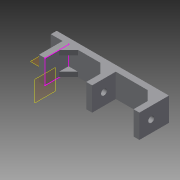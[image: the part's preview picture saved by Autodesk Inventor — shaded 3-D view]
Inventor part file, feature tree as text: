
AUTODESK INVENTOR PART (.ipt)
format: ipt  version: 2013 (Build 170138000, 138)  size: 146,944 bytes
history: native  units: in
note: dims shown in document units (in); Inventor stores cm internally (conversion verified against a paired STEP export)
features: sketch x6, extrude x5, plane x2
ambient origin geometry x8: Origin, YZ Plane, XZ Plane, XY Plane, X Axis, Y Axis, Z Axis, Center Point
bodies: Solid1 (feature_tree)
feature tree (13):
  extrude  "Extrusion1"  Depth=4.75in
  plane  "Work Plane1"
  extrude  "Extrusion3"  Depth=0.25in TaperAngle=0.0deg
  plane  "Work Plane2"
  sketch  "Sketch4"  dims[d8=0.5in d9=0.25in]
  extrude  "Extrusion4"  Depth=0.25in
  extrude  "Extrusion5"  Depth=1.75in
  extrude  "Extrusion6"  Depth=1.0in
  sketch  "Sketch1"  dims[d0=1.0in d1=4.75in]
  sketch  "Sketch3"  dims[d2=1.0in d3=0.25in d4=0.0in]
  sketch  "Sketch5"  dims[d10=1.0in d11=1.75in]
  sketch  "Sketch6"  dims[d12=0.25in d13=1.0in]
  sketch  "Sketch7"  dims[d14=1.75in d15=1.0in d16=0.0in d17=0.75in d18=0.5in d19=0.25in d20=3.0in d21=0.0in d22=0.4in d23=0.4in d24=0.4in d25=0.4in d26=0.2in d27=0.0in d28=0.4in d29=0.4in d30=0.4in d31=0.4in d32=0.2in d33=0.0in]
